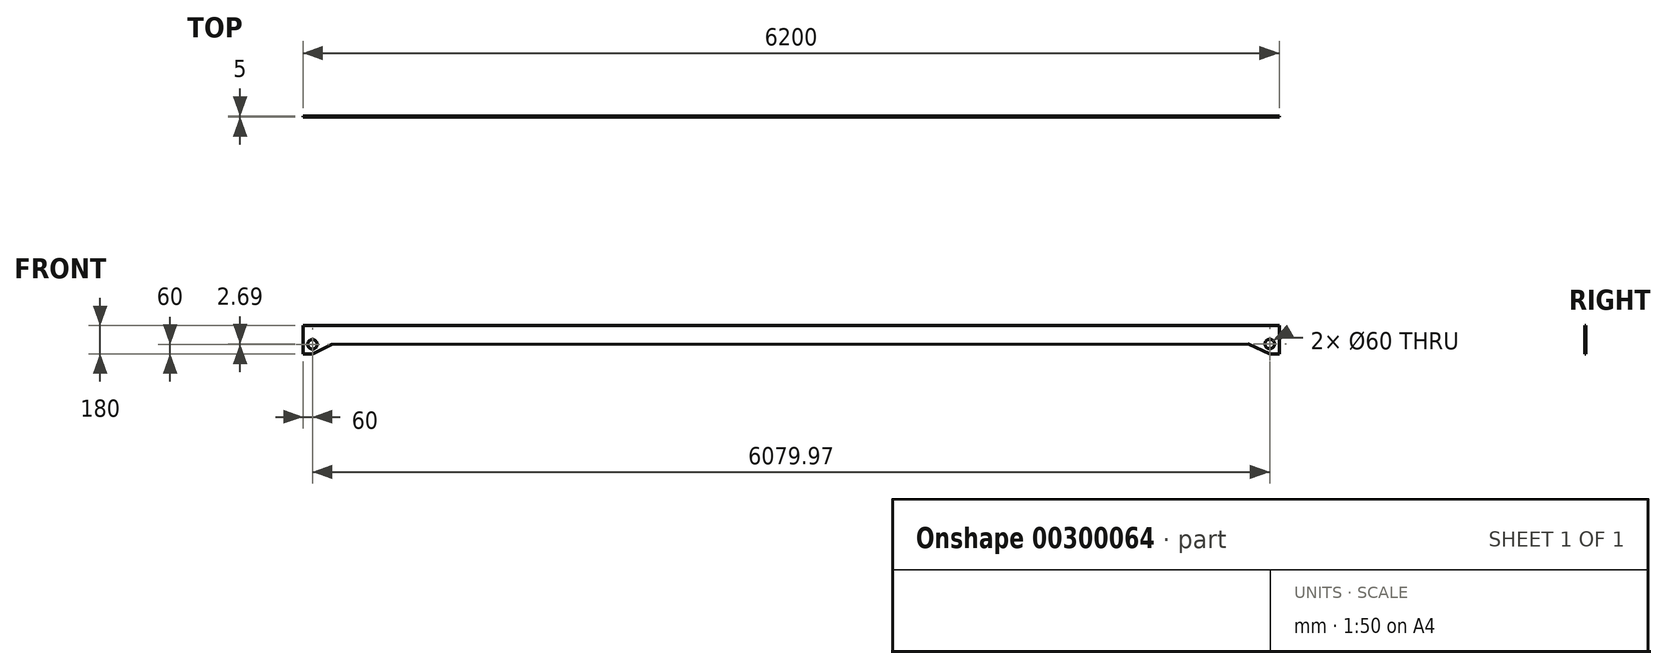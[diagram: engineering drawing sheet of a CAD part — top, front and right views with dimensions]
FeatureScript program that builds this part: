
annotation { "Feature Type Name" : "Feature", "Feature Type Description" : "" }
export const myFeature = defineFeature(function(context is Context, id is Id, definition is map)
    precondition{}
    {
        {
            var Q0;
            Q0=qCreatedBy(makeId("Front.planeOp"),FACE);
            var sketch = newSketch(context, id + "F0", { "sketchPlane" : qUnion([Q0])});
            skLineSegment(sketch, "E0", {"start": v(0, 0) * mm, "end": v(-6200, 0) * mm});
            skLineSegment(sketch, "E1", {"start": v(-6200, 0) * mm, "end": v(-6200, -180) * mm});
            skLineSegment(sketch, "E2", {"start": v(-6200, -180) * mm, "end": v(-6140, -180) * mm});
            skLineSegment(sketch, "E3", {"start": v(-6020, -120) * mm, "end": v(-6140, -180) * mm});
            skLineSegment(sketch, "E4", {"start": v(0, 0) * mm, "end": v(0, -180) * mm});
            skLineSegment(sketch, "E5", {"start": v(0, -180) * mm, "end": v(-60, -180) * mm});
            skLineSegment(sketch, "E6", {"start": v(-196.8, -117.31) * mm, "end": v(-60, -180) * mm});
            skLineSegment(sketch, "E7", {"start": v(-196.8, -117.31) * mm, "end": v(-6020, -120) * mm});
            skSolve(sketch);
        }
        {
            var Q0;
            Q0 = qSketchRegion(id + "F0", true);
            extrude(context, id + "F1", {"entities" : qUnion([Q0]), "depth" : 5 * mm});
        }
        {
            var Q0;
            Q0=makeQuery(id+"F1.opExtrude","CAP_FACE",FACE,{"disambiguationData":[OSD([sQuery(id+"F0.wireOp",EDGE,"E0"),sQuery(id+"F0.wireOp",EDGE,"E1"),sQuery(id+"F0.wireOp",EDGE,"E2"),sQuery(id+"F0.wireOp",EDGE,"E3"),sQuery(id+"F0.wireOp",EDGE,"E4"),sQuery(id+"F0.wireOp",EDGE,"E5"),sQuery(id+"F0.wireOp",EDGE,"E6"),sQuery(id+"F0.wireOp",EDGE,"E7")])],"isStart":false});
            var sketch = newSketch(context, id + "F2", { "sketchPlane" : qUnion([Q0])});
            skLineSegment(sketch, "E8", {"start": v(-6140, -180) * mm, "end": v(-6140, -120) * mm});
            skLineSegment(sketch, "E9", {"start": v(-60, -180) * mm, "end": v(-60.03, -117.31) * mm});
            skSolve(sketch);
        }
        {
            var Q0;
            Q0=sQuery(id+"F2.wireOp",VERTEX,"E9.end");
            var Q1;
            Q1=sQuery(id+"F2.wireOp",VERTEX,"E8.end");
            var Q2;
            Q2=makeQuery(id+"F1.opExtrude","SWEPT_BODY",BODY,{"disambiguationData":[OSD([sQuery(id+"F0.wireOp",EDGE,"E0"),sQuery(id+"F0.wireOp",EDGE,"E1"),sQuery(id+"F0.wireOp",EDGE,"E2"),sQuery(id+"F0.wireOp",EDGE,"E3"),sQuery(id+"F0.wireOp",EDGE,"E4"),sQuery(id+"F0.wireOp",EDGE,"E5"),sQuery(id+"F0.wireOp",EDGE,"E6"),sQuery(id+"F0.wireOp",EDGE,"E7")])]});
            hole(context, id + "F3", {"style" : HoleStyle.SIMPLE, "endStyle" : HoleEndStyle.THROUGH, "holeDiameter" : 60 * mm, "tappedDepth" : 12 * mm, "tapClearance" : 3, "locations" : qUnion([Q0, Q1]), "scope" : qUnion([Q2])});
        }
    });
